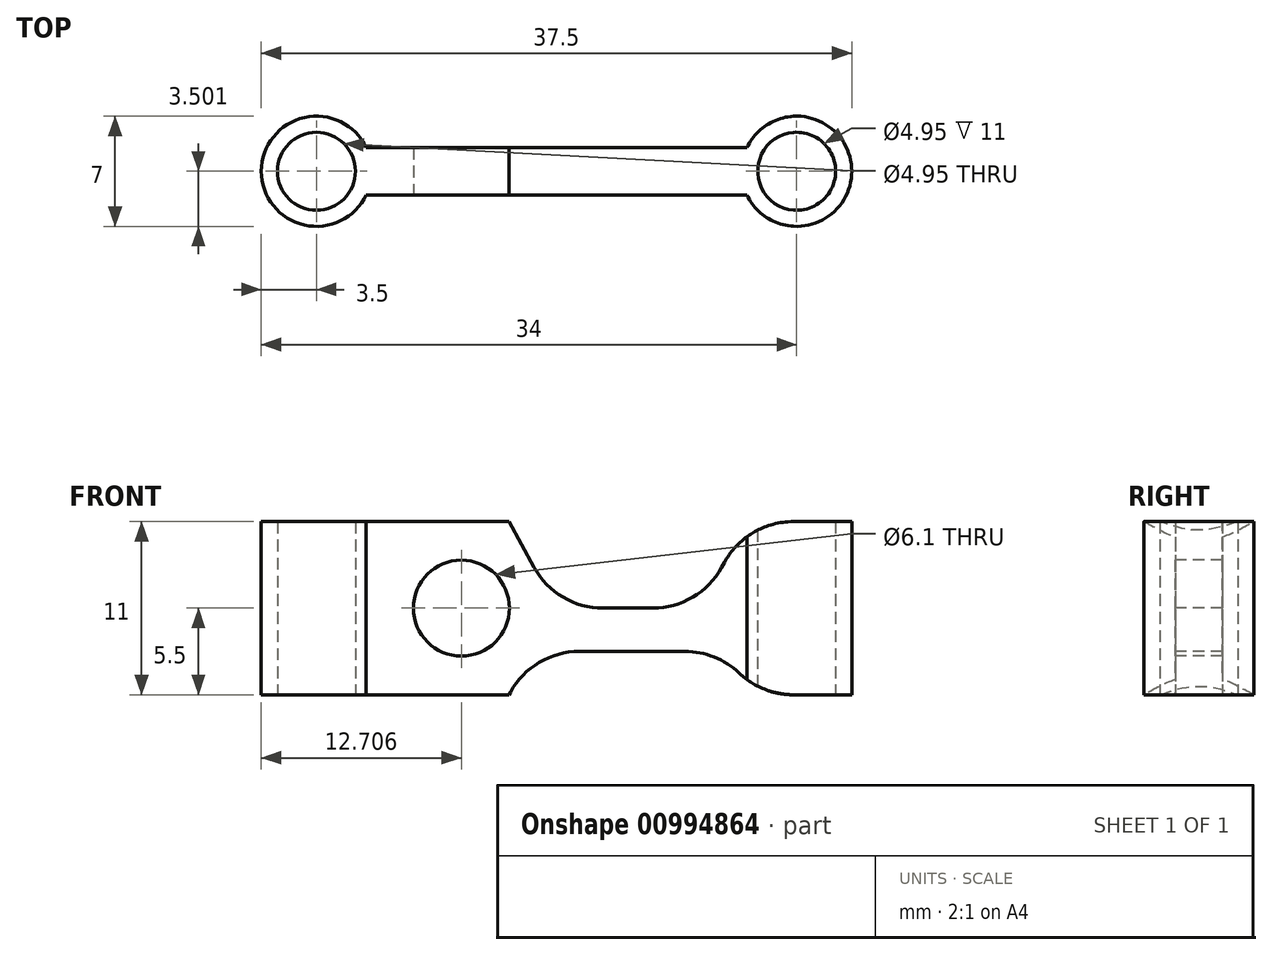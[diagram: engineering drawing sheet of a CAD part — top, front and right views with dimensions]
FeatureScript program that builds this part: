
annotation { "Feature Type Name" : "Feature", "Feature Type Description" : "" }
export const myFeature = defineFeature(function(context is Context, id is Id, definition is map)
    precondition{}
    {
        {
            var Q0;
            Q0=qCreatedBy(makeId("Top.planeOp"),FACE);
            var sketch = newSketch(context, id + "F0", { "sketchPlane" : qUnion([Q0])});
            skCircle(sketch, "E0", {"center": v(15.25, 12.6) * mm, "radius": 2.48 * mm});
            skLineSegment(sketch, "E1.bottom", {"start": v(15.25, 11.1) * mm, "end": v(-15.25, 11.1) * mm});
            skLineSegment(sketch, "E1.top", {"start": v(15.25, 14.1) * mm, "end": v(-15.25, 14.1) * mm});
            skLineSegment(sketch, "E1.left", {"start": v(15.25, 11.1) * mm, "end": v(15.25, 14.1) * mm});
            skLineSegment(sketch, "E1.right", {"start": v(-15.25, 11.1) * mm, "end": v(-15.25, 14.1) * mm});
            skPoint(sketch, "E1.middle", {"position": v(0, 12.6) * mm});
            skCircle(sketch, "E2", {"center": v(-15.25, 12.6) * mm, "radius": 2.48 * mm});
            skCircle(sketch, "E3", {"center": v(15.25, 12.6) * mm, "radius": 3.5 * mm});
            skCircle(sketch, "E4", {"center": v(-15.25, 12.6) * mm, "radius": 3.5 * mm});
            skSolve(sketch);
        }
        {
            var Q0;
            Q0 = qSketchRegion(id + "F0", true);
            extrude(context, id + "F1", {"entities" : qUnion([Q0]), "depth" : 11 * mm, "offsetDistance" : 25 * mm});
        }
        {
            var Q0;
            Q0=makeQuery(id+"F1.opExtrude","SWEPT_FACE",FACE,{"disambiguationData":[OSD([sQuery(id+"F0.wireOp",EDGE,"E1.bottom")])]});
            var sketch = newSketch(context, id + "F2", { "sketchPlane" : qUnion([Q0])});
            skLineSegment(sketch, "E5", {"start": v(0, 11) * mm, "end": v(0, 0) * mm, "construction": true});
            skCircle(sketch, "E6", {"center": v(-6.04, 5.5) * mm, "radius": 3.05 * mm});
            skLineSegment(sketch, "E7", {"start": v(0, 5.5) * mm, "end": v(-12.09, 5.5) * mm, "construction": true});
            skLineSegment(sketch, "E8", {"start": v(-6.04, 11) * mm, "end": v(0, 11) * mm, "construction": true});
            skLineSegment(sketch, "E9", {"start": v(-3.02, 11) * mm, "end": v(0, 5.5) * mm});
            skLineSegment(sketch, "E10", {"start": v(12.09, 11) * mm, "end": v(9.07, 5.5) * mm});
            skLineSegment(sketch, "E11", {"start": v(9.07, 5.5) * mm, "end": v(0, 5.5) * mm});
            skLineSegment(sketch, "E12", {"start": v(-3.02, 11) * mm, "end": v(12.09, 11) * mm});
            skLineSegment(sketch, "E13.MirrorCS", {"start": v(-3.02, 0) * mm, "end": v(12.09, 0) * mm});
            skLineSegment(sketch, "E14.MirrorCS", {"start": v(-3.02, 0) * mm, "end": v(0, 5.5) * mm});
            skLineSegment(sketch, "E15.MirrorCS", {"start": v(12.09, 0) * mm, "end": v(9.07, 5.5) * mm});
            skLineSegment(sketch, "E16", {"start": v(-1.51, 2.75) * mm, "end": v(10.58, 2.75) * mm});
            skSolve(sketch);
        }
        {
            var Q0;
            Q0=makeQuery(id+"F2.imprint","IMPRINT",FACE,{"disambiguationData":[TD([[makeQuery(id+"F2.imprint","IMPRINT",EDGE,{"derivedFrom":sQuery(id+"F2.wireOp",EDGE,"E6")}),1.0]])]});
            var Q1;
            Q1=makeQuery(id+"F2.imprint","IMPRINT",FACE,{"disambiguationData":[TD([[makeQuery(id+"F2.imprint","IMPRINT",EDGE,{"derivedFrom":sQuery(id+"F2.wireOp",EDGE,"E9")}),1.0]])]});
            var Q2;
            Q2=makeQuery(id+"F2.imprint","IMPRINT",FACE,{"disambiguationData":[TD([[makeQuery(id+"F2.imprint","IMPRINT",EDGE,{"derivedFrom":sQuery(id+"F2.wireOp",EDGE,"E13.MirrorCS")}),-1.0]])]});
            extrude(context, id + "F3", {"entities" : qUnion([Q0, Q1, Q2]), "operationType" : NewBodyOperationType.REMOVE, "endBound" : BoundingType.UP_TO_NEXT, "oppositeDirection" : true, "depth" : 25 * mm, "offsetDistance" : 25 * mm});
        }
        {
            var Q0;
            Q0=makeQuery(id+"F3.boolean.opBoolean","COPY",EDGE,{"derivedFrom":makeQuery(id+"F3.opExtrude","SWEPT_EDGE",EDGE,{"disambiguationData":[OSD([sQuery(id+"F0.wireOp",EDGE,"E1.bottom"),sQuery(id+"F2.wireOp",EDGE,"E9"),sQuery(id+"F2.wireOp",EDGE,"E12")])]})});
            var Q1;
            {var subQ0=sQuery(id+"F2.wireOp",EDGE,"E9");Q1=qUnion([makeQuery(id+"F3.boolean.opBoolean","COPY",EDGE,{"derivedFrom":makeQuery(id+"F3.opExtrude","SWEPT_EDGE",EDGE,{"disambiguationData":[OSD([sQuery(id+"F0.wireOp",EDGE,"E1.bottom"),subQ0,sQuery(id+"F2.wireOp",EDGE,"E12")])]})}),makeQuery(id+"F3.boolean.opBoolean","COPY",EDGE,{"derivedFrom":makeQuery(id+"F3.opExtrude","SWEPT_EDGE",EDGE,{"disambiguationData":[OSD([subQ0,sQuery(id+"F2.wireOp",EDGE,"E14.MirrorCS"),sQuery(id+"F2.wireOp",EDGE,"E11")])]})})]);}
            var Q2;
            Q2=makeQuery(id+"F3.boolean.opBoolean","COPY",EDGE,{"derivedFrom":makeQuery(id+"F3.opExtrude","SWEPT_EDGE",EDGE,{"disambiguationData":[OSD([sQuery(id+"F2.wireOp",EDGE,"E10"),sQuery(id+"F2.wireOp",EDGE,"E15.MirrorCS"),sQuery(id+"F2.wireOp",EDGE,"E11")])]})});
            var Q3;
            {var subQ0=sQuery(id+"F0.wireOp",EDGE,"E3");var subQ1=sQuery(id+"F0.wireOp",EDGE,"E1.top");Q3=makeQuery(id+"F3.boolean.opBoolean","COPY",EDGE,{"derivedFrom":makeQuery(id+"F3.opExtrude","SWEPT_EDGE",EDGE,{"disambiguationData":[OSD([subQ1,subQ0]),TDD([makeQuery(id+"F1.opExtrude","CAP_VERTEX",VERTEX,{"disambiguationData":[OSD([subQ1,subQ0])],"isStart":false})])]})});}
            var Q4;
            Q4=makeQuery(id+"F3.boolean.opBoolean","COPY",EDGE,{"derivedFrom":makeQuery(id+"F3.opExtrude","SWEPT_EDGE",EDGE,{"disambiguationData":[OSD([sQuery(id+"F0.wireOp",EDGE,"E1.bottom"),sQuery(id+"F2.wireOp",EDGE,"E13.MirrorCS"),sQuery(id+"F2.wireOp",EDGE,"E14.MirrorCS")])]})});
            var Q5;
            {var subQ0=sQuery(id+"F0.wireOp",EDGE,"E3");var subQ1=sQuery(id+"F0.wireOp",EDGE,"E1.top");Q5=makeQuery(id+"F3.boolean.opBoolean","COPY",EDGE,{"derivedFrom":makeQuery(id+"F3.opExtrude","SWEPT_EDGE",EDGE,{"disambiguationData":[OSD([subQ1,subQ0]),TDD([makeQuery(id+"F1.opExtrude","CAP_VERTEX",VERTEX,{"disambiguationData":[OSD([subQ1,subQ0])],"isStart":true})])]})});}
            fillet(context, id + "F4", {"entities" : qUnion([Q0, Q1, Q2, Q3, Q4, Q5]), "radius" : 5 * mm, "tangentPropagation" : true, "allowEdgeOverflow" : false});
        }
        {
            var Q0;
            Q0=makeQuery(id+"F3.boolean.opBoolean","COPY",EDGE,{"derivedFrom":makeQuery(id+"F3.opExtrude","SWEPT_EDGE",EDGE,{"disambiguationData":[OSD([sQuery(id+"F2.wireOp",EDGE,"E15.MirrorCS"),sQuery(id+"F2.wireOp",EDGE,"E16")])]})});
            var Q1;
            Q1=makeQuery(id+"F3.boolean.opBoolean","COPY",EDGE,{"derivedFrom":makeQuery(id+"F3.opExtrude","SWEPT_EDGE",EDGE,{"disambiguationData":[OSD([sQuery(id+"F2.wireOp",EDGE,"E14.MirrorCS"),sQuery(id+"F2.wireOp",EDGE,"E16")])]})});
            fillet(context, id + "F5", {"entities" : qUnion([Q0, Q1]), "radius" : 5 * mm, "tangentPropagation" : true, "allowEdgeOverflow" : false});
        }
    });
